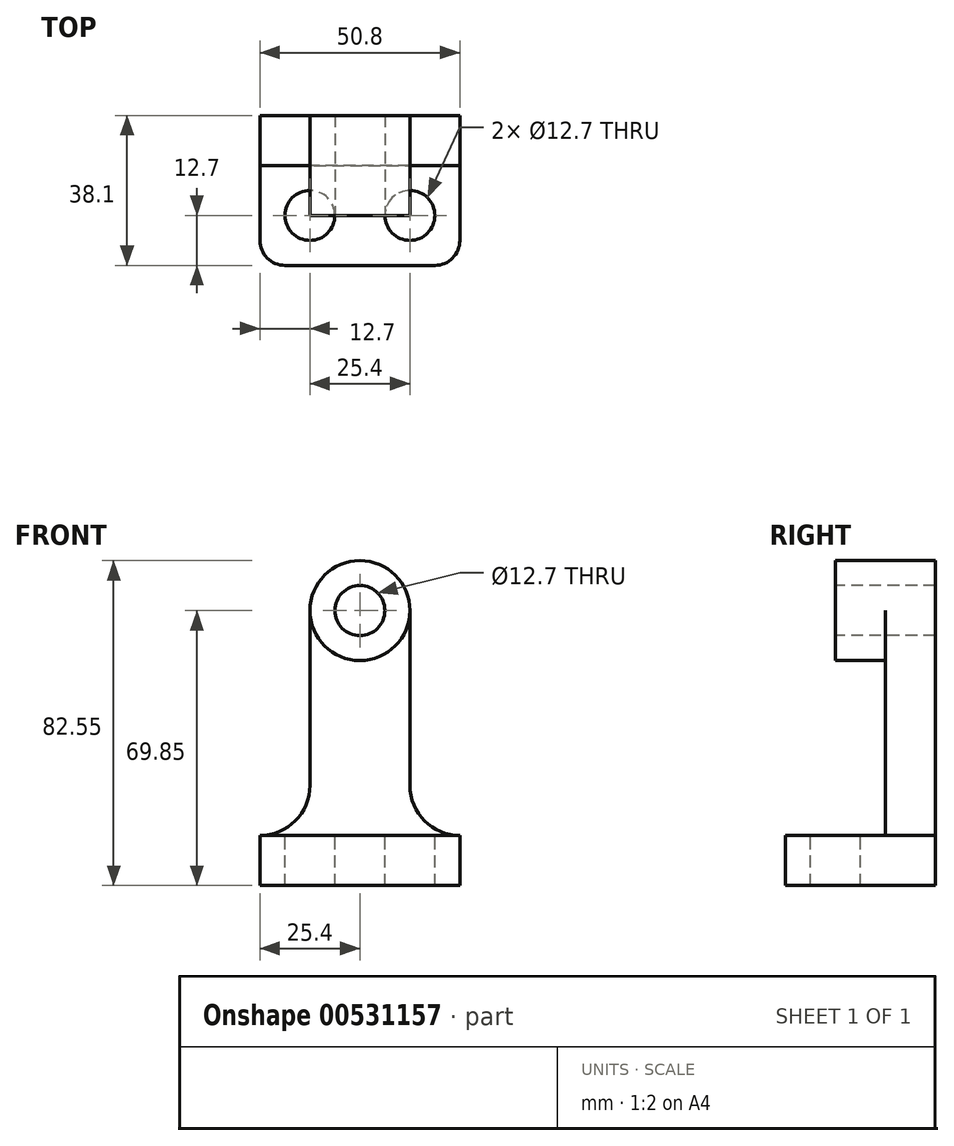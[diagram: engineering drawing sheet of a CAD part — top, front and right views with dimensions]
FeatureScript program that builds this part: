
annotation { "Feature Type Name" : "Feature", "Feature Type Description" : "" }
export const myFeature = defineFeature(function(context is Context, id is Id, definition is map)
    precondition{}
    {
        {
            var Q0;
            Q0=qCreatedBy(makeId("Top.planeOp"),FACE);
            var sketch = newSketch(context, id + "F0", { "sketchPlane" : qUnion([Q0])});
            skLineSegment(sketch, "E0.bottom", {"start": v(0, 0) * mm, "end": v(50.8, 0) * mm});
            skLineSegment(sketch, "E0.top", {"start": v(0, 38.1) * mm, "end": v(50.8, 38.1) * mm});
            skLineSegment(sketch, "E0.left", {"start": v(0, 0) * mm, "end": v(0, 38.1) * mm});
            skLineSegment(sketch, "E0.right", {"start": v(50.8, 0) * mm, "end": v(50.8, 38.1) * mm});
            skSolve(sketch);
        }
        {
            var Q0;
            Q0 = qSketchRegion(id + "F0", true);
            extrude(context, id + "F1", {"entities" : qUnion([Q0]), "depth" : 12.7 * mm, "offsetDistance" : 25.4 * mm});
        }
        {
            var Q0;
            Q0=makeQuery(id+"F1.opExtrude","SWEPT_EDGE",EDGE,{"disambiguationData":[OSD([sQuery(id+"F0.wireOp",EDGE,"E0.bottom"),sQuery(id+"F0.wireOp",EDGE,"E0.left")])]});
            var Q1;
            Q1=makeQuery(id+"F1.opExtrude","SWEPT_EDGE",EDGE,{"disambiguationData":[OSD([sQuery(id+"F0.wireOp",EDGE,"E0.bottom"),sQuery(id+"F0.wireOp",EDGE,"E0.right")])]});
            fillet(context, id + "F2", {"entities" : qUnion([Q0, Q1]), "radius" : 6.35 * mm, "tangentPropagation" : true, "allowEdgeOverflow" : false});
        }
        {
            var Q0;
            Q0=makeQuery(id+"F1.opExtrude","CAP_FACE",FACE,{"disambiguationData":[OSD([sQuery(id+"F0.wireOp",EDGE,"E0.bottom"),sQuery(id+"F0.wireOp",EDGE,"E0.top"),sQuery(id+"F0.wireOp",EDGE,"E0.left"),sQuery(id+"F0.wireOp",EDGE,"E0.right")])],"isStart":false});
            var sketch = newSketch(context, id + "F3", { "sketchPlane" : qUnion([Q0])});
            skLineSegment(sketch, "E1.bottom", {"start": v(0, 0) * mm, "end": v(12.7, 0) * mm, "construction": true});
            skLineSegment(sketch, "E1.top", {"start": v(0, 12.7) * mm, "end": v(12.7, 12.7) * mm, "construction": true});
            skLineSegment(sketch, "E1.left", {"start": v(0, 0) * mm, "end": v(0, 12.7) * mm, "construction": true});
            skLineSegment(sketch, "E1.right", {"start": v(12.7, 0) * mm, "end": v(12.7, 12.7) * mm, "construction": true});
            skLineSegment(sketch, "E2.bottom", {"start": v(50.8, 0) * mm, "end": v(38.1, 0) * mm, "construction": true});
            skLineSegment(sketch, "E2.top", {"start": v(50.8, 12.7) * mm, "end": v(38.1, 12.7) * mm, "construction": true});
            skLineSegment(sketch, "E2.left", {"start": v(50.8, 0) * mm, "end": v(50.8, 12.7) * mm, "construction": true});
            skLineSegment(sketch, "E2.right", {"start": v(38.1, 0) * mm, "end": v(38.1, 12.7) * mm, "construction": true});
            skCircle(sketch, "E3", {"center": v(12.7, 12.7) * mm, "radius": 6.35 * mm});
            skCircle(sketch, "E4", {"center": v(38.1, 12.7) * mm, "radius": 6.35 * mm});
            skSolve(sketch);
        }
        {
            var Q0;
            Q0=makeQuery(id+"F3.imprint","IMPRINT",FACE,{"disambiguationData":[TD([[makeQuery(id+"F3.imprint","IMPRINT",EDGE,{"derivedFrom":sQuery(id+"F3.wireOp",EDGE,"E3")}),1.0]])]});
            var Q1;
            Q1=makeQuery(id+"F3.imprint","IMPRINT",FACE,{"disambiguationData":[TD([[makeQuery(id+"F3.imprint","IMPRINT",EDGE,{"derivedFrom":sQuery(id+"F3.wireOp",EDGE,"E4")}),1.0]])]});
            extrude(context, id + "F4", {"entities" : qUnion([Q0, Q1]), "operationType" : NewBodyOperationType.REMOVE, "oppositeDirection" : true, "depth" : 25.4 * mm, "offsetDistance" : 25.4 * mm});
        }
        {
            var Q0;
            Q0=makeQuery(id+"F1.opExtrude","CAP_FACE",FACE,{"disambiguationData":[OSD([sQuery(id+"F0.wireOp",EDGE,"E0.bottom"),sQuery(id+"F0.wireOp",EDGE,"E0.top"),sQuery(id+"F0.wireOp",EDGE,"E0.left"),sQuery(id+"F0.wireOp",EDGE,"E0.right")])],"isStart":false});
            var sketch = newSketch(context, id + "F5", { "sketchPlane" : qUnion([Q0])});
            skLineSegment(sketch, "E5.bottom", {"start": v(0, 38.1) * mm, "end": v(12.7, 38.1) * mm, "construction": true});
            skLineSegment(sketch, "E5.top", {"start": v(0, 25.4) * mm, "end": v(12.7, 25.4) * mm, "construction": true});
            skLineSegment(sketch, "E5.left", {"start": v(0, 38.1) * mm, "end": v(0, 25.4) * mm, "construction": true});
            skLineSegment(sketch, "E5.right", {"start": v(12.7, 38.1) * mm, "end": v(12.7, 25.4) * mm, "construction": true});
            skLineSegment(sketch, "E6.bottom", {"start": v(50.8, 38.1) * mm, "end": v(38.1, 38.1) * mm, "construction": true});
            skLineSegment(sketch, "E6.top", {"start": v(50.8, 25.4) * mm, "end": v(38.1, 25.4) * mm, "construction": true});
            skLineSegment(sketch, "E6.left", {"start": v(50.8, 38.1) * mm, "end": v(50.8, 25.4) * mm, "construction": true});
            skLineSegment(sketch, "E6.right", {"start": v(38.1, 38.1) * mm, "end": v(38.1, 25.4) * mm, "construction": true});
            skLineSegment(sketch, "E7.bottom", {"start": v(12.7, 38.1) * mm, "end": v(38.1, 38.1) * mm});
            skLineSegment(sketch, "E7.top", {"start": v(12.7, 25.4) * mm, "end": v(38.1, 25.4) * mm});
            skLineSegment(sketch, "E7.left", {"start": v(12.7, 38.1) * mm, "end": v(12.7, 25.4) * mm});
            skLineSegment(sketch, "E7.right", {"start": v(38.1, 38.1) * mm, "end": v(38.1, 25.4) * mm});
            skSolve(sketch);
        }
        {
            var Q0;
            Q0=makeQuery(id+"F5.imprint","IMPRINT",FACE,{"disambiguationData":[TD([[makeQuery(id+"F5.imprint","IMPRINT",EDGE,{"derivedFrom":sQuery(id+"F5.wireOp",EDGE,"E7.bottom")}),-1.0]])]});
            extrude(context, id + "F6", {"entities" : qUnion([Q0]), "operationType" : NewBodyOperationType.ADD, "depth" : 69.85 * mm, "offsetDistance" : 25.4 * mm});
        }
        {
            var Q0;
            Q0=makeQuery(id+"F6.opExtrude","CAP_EDGE",EDGE,{"disambiguationData":[OSD([sQuery(id+"F5.wireOp",EDGE,"E7.right")])],"isStart":false});
            var Q1;
            Q1=makeQuery(id+"F6.opExtrude","CAP_EDGE",EDGE,{"disambiguationData":[OSD([sQuery(id+"F5.wireOp",EDGE,"E7.left")])],"isStart":false});
            fillet(context, id + "F7", {"entities" : qUnion([Q0, Q1]), "radius" : 12.7 * mm, "tangentPropagation" : true, "allowEdgeOverflow" : false});
        }
        {
            var Q0;
            Q0=makeQuery(id+"F1.opExtrude","CAP_FACE",FACE,{"disambiguationData":[OSD([sQuery(id+"F0.wireOp",EDGE,"E0.bottom"),sQuery(id+"F0.wireOp",EDGE,"E0.top"),sQuery(id+"F0.wireOp",EDGE,"E0.left"),sQuery(id+"F0.wireOp",EDGE,"E0.right")])],"isStart":false});
            var sketch = newSketch(context, id + "F8", { "sketchPlane" : qUnion([Q0])});
            skLineSegment(sketch, "E8.bottom", {"start": v(50.8, 38.1) * mm, "end": v(38.1, 38.1) * mm});
            skLineSegment(sketch, "E8.top", {"start": v(50.8, 25.4) * mm, "end": v(38.1, 25.4) * mm});
            skLineSegment(sketch, "E8.left", {"start": v(50.8, 38.1) * mm, "end": v(50.8, 25.4) * mm});
            skLineSegment(sketch, "E8.right", {"start": v(38.1, 38.1) * mm, "end": v(38.1, 25.4) * mm});
            skLineSegment(sketch, "E9.bottom", {"start": v(0, 38.1) * mm, "end": v(12.7, 38.1) * mm});
            skLineSegment(sketch, "E9.top", {"start": v(0, 25.4) * mm, "end": v(12.7, 25.4) * mm});
            skLineSegment(sketch, "E9.left", {"start": v(0, 38.1) * mm, "end": v(0, 25.4) * mm});
            skLineSegment(sketch, "E9.right", {"start": v(12.7, 38.1) * mm, "end": v(12.7, 25.4) * mm});
            skSolve(sketch);
        }
        {
            var Q0;
            Q0=makeQuery(id+"F8.imprint","IMPRINT",FACE,{"disambiguationData":[TD([[makeQuery(id+"F8.imprint","IMPRINT",EDGE,{"derivedFrom":sQuery(id+"F8.wireOp",EDGE,"E9.bottom")}),-1.0]])]});
            var Q1;
            Q1=makeQuery(id+"F8.imprint","IMPRINT",FACE,{"disambiguationData":[TD([[makeQuery(id+"F8.imprint","IMPRINT",EDGE,{"derivedFrom":sQuery(id+"F8.wireOp",EDGE,"E8.bottom")}),-1.0]])]});
            extrude(context, id + "F9", {"entities" : qUnion([Q0, Q1]), "operationType" : NewBodyOperationType.ADD, "depth" : 12.7 * mm, "offsetDistance" : 25.4 * mm});
        }
        {
            var Q0;
            Q0=makeQuery(id+"F9.boolean.opBoolean","MERGE",FACE,{"derivedFrom":[makeQuery(id+"F6.opExtrude","SWEPT_FACE",FACE,{"disambiguationData":[OSD([sQuery(id+"F5.wireOp",EDGE,"E7.top")])]}),makeQuery(id+"F9.opExtrude","SWEPT_FACE",FACE,{"disambiguationData":[OSD([sQuery(id+"F8.wireOp",EDGE,"E8.top")])]}),makeQuery(id+"F9.opExtrude","SWEPT_FACE",FACE,{"disambiguationData":[OSD([sQuery(id+"F8.wireOp",EDGE,"E9.top")])]})]});
            var sketch = newSketch(context, id + "F10", { "sketchPlane" : qUnion([Q0])});
            skArc(sketch, "E10", {"start": v(0, 12.7) * mm, "mid": v(8.98, 16.42) * mm, "end": v(12.7, 25.4) * mm});
            skArc(sketch, "E11", {"start": v(38.1, 25.4) * mm, "mid": v(41.82, 16.42) * mm, "end": v(50.8, 12.7) * mm});
            skSolve(sketch);
        }
        {
            var Q0;
            Q0=makeQuery(id+"F10.imprint","IMPRINT",FACE,{"disambiguationData":[TD([[makeQuery(id+"F10.imprint","IMPRINT",EDGE,{"derivedFrom":sQuery(id+"F10.wireOp",EDGE,"E10")}),1.0]])]});
            var Q1;
            Q1=makeQuery(id+"F10.imprint","IMPRINT",FACE,{"disambiguationData":[TD([[makeQuery(id+"F10.imprint","IMPRINT",EDGE,{"derivedFrom":sQuery(id+"F10.wireOp",EDGE,"E11")}),1.0]])]});
            extrude(context, id + "F11", {"entities" : qUnion([Q0, Q1]), "operationType" : NewBodyOperationType.REMOVE, "oppositeDirection" : true, "depth" : 25.4 * mm, "offsetDistance" : 25.4 * mm});
        }
        {
            var Q0;
            Q0=makeQuery(id+"F9.boolean.opBoolean","MERGE",FACE,{"derivedFrom":[makeQuery(id+"F6.opExtrude","SWEPT_FACE",FACE,{"disambiguationData":[OSD([sQuery(id+"F5.wireOp",EDGE,"E7.top")])]}),makeQuery(id+"F9.opExtrude","SWEPT_FACE",FACE,{"disambiguationData":[OSD([sQuery(id+"F8.wireOp",EDGE,"E8.top")])]}),makeQuery(id+"F9.opExtrude","SWEPT_FACE",FACE,{"disambiguationData":[OSD([sQuery(id+"F8.wireOp",EDGE,"E9.top")])]})]});
            var sketch = newSketch(context, id + "F12", { "sketchPlane" : qUnion([Q0])});
            skCircle(sketch, "E12", {"center": v(25.4, 69.85) * mm, "radius": 12.7 * mm});
            skSolve(sketch);
        }
        {
            var Q0;
            Q0 = qSketchRegion(id + "F12", true);
            extrude(context, id + "F13", {"entities" : qUnion([Q0]), "operationType" : NewBodyOperationType.ADD, "depth" : 12.7 * mm, "offsetDistance" : 25.4 * mm});
        }
        {
            var Q0;
            Q0=makeQuery(id+"F13.opExtrude","CAP_FACE",FACE,{"disambiguationData":[OSD([sQuery(id+"F12.wireOp",EDGE,"E12")])],"isStart":false});
            var sketch = newSketch(context, id + "F14", { "sketchPlane" : qUnion([Q0])});
            skCircle(sketch, "E13", {"center": v(25.4, 69.85) * mm, "radius": 6.35 * mm});
            skSolve(sketch);
        }
        {
            var Q0;
            Q0=makeQuery(id+"F14.imprint","IMPRINT",FACE,{"disambiguationData":[TD([[makeQuery(id+"F14.imprint","IMPRINT",EDGE,{"derivedFrom":sQuery(id+"F14.wireOp",EDGE,"E13")}),1.0]])]});
            extrude(context, id + "F15", {"entities" : qUnion([Q0]), "operationType" : NewBodyOperationType.REMOVE, "oppositeDirection" : true, "depth" : 25.4 * mm, "offsetDistance" : 25.4 * mm});
        }
    });
